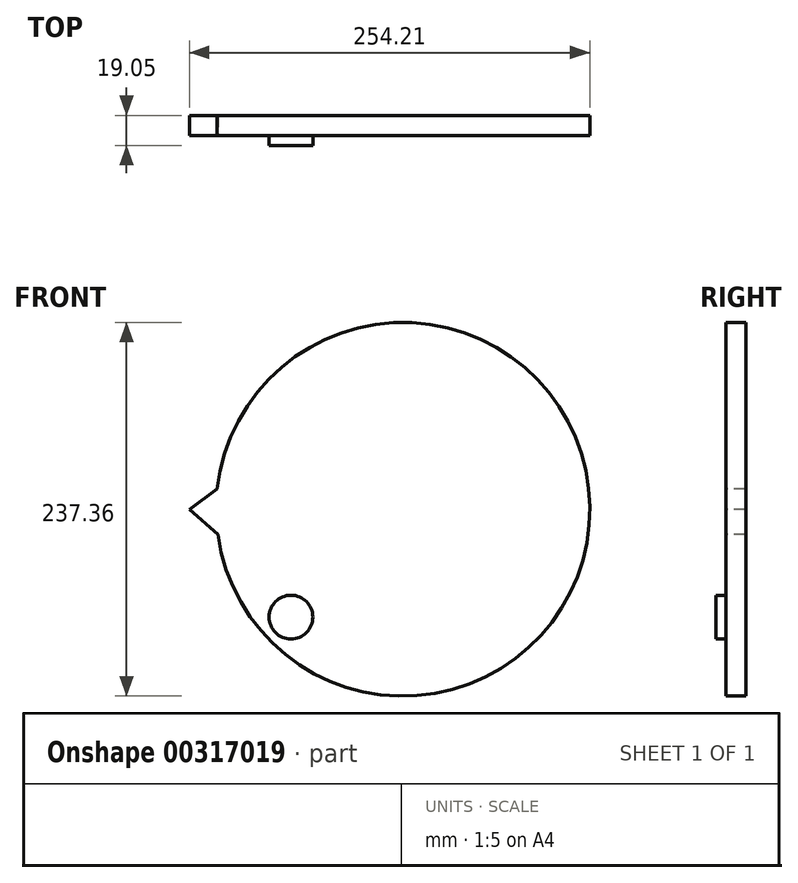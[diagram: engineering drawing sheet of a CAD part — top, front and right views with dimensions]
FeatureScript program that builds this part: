
annotation { "Feature Type Name" : "Feature", "Feature Type Description" : "" }
export const myFeature = defineFeature(function(context is Context, id is Id, definition is map)
    precondition{}
    {
        {
            var Q0;
            Q0=qCreatedBy(makeId("Front.planeOp"),FACE);
            var sketch = newSketch(context, id + "F0", { "sketchPlane" : qUnion([Q0])});
            skCircle(sketch, "E0", {"center": v(0, 0) * mm, "radius": 118.68 * mm});
            skSolve(sketch);
        }
        {
            var Q0;
            Q0 = qSketchRegion(id + "F0", true);
            extrude(context, id + "F1", {"entities" : qUnion([Q0]), "depth" : 12.7 * mm, "symmetric" : true});
        }
        {
            var Q0;
            Q0=makeQuery(id+"F1.opExtrude","CAP_FACE",FACE,{"disambiguationData":[OSD([sQuery(id+"F0.wireOp",EDGE,"E0")])],"isStart":false});
            var sketch = newSketch(context, id + "F2", { "sketchPlane" : qUnion([Q0])});
            skCircle(sketch, "E1", {"center": v(-71.15, -68.46) * mm, "radius": 13.87 * mm});
            skSolve(sketch);
        }
        {
            var Q0;
            Q0 = qSketchRegion(id + "F2", true);
            extrude(context, id + "F3", {"entities" : qUnion([Q0]), "operationType" : NewBodyOperationType.ADD, "depth" : 6.35 * mm});
        }
        {
            var Q0;
            Q0=makeQuery(id+"F1.opExtrude","CAP_FACE",FACE,{"disambiguationData":[OSD([sQuery(id+"F0.wireOp",EDGE,"E0")])],"isStart":false});
            var sketch = newSketch(context, id + "F4", { "sketchPlane" : qUnion([Q0])});
            skLineSegment(sketch, "E2", {"start": v(-117.58, -16.11) * mm, "end": v(-135.53, 0) * mm});
            skLineSegment(sketch, "E3", {"start": v(-135.53, 0) * mm, "end": v(-117.97, 12.9) * mm});
            skArc(sketch, "E4.0", {"start": v(-117.97, 12.9) * mm, "mid": v(-118.67, -1.61) * mm, "end": v(-117.58, -16.11) * mm});
            skSolve(sketch);
        }
        {
            var Q0;
            Q0 = qSketchRegion(id + "F4", true);
            var Q1;
            Q1=makeQuery(id+"F1.opExtrude","CAP_FACE",FACE,{"disambiguationData":[OSD([sQuery(id+"F0.wireOp",EDGE,"E0")])],"isStart":true});
            extrude(context, id + "F5", {"entities" : qUnion([Q0]), "operationType" : NewBodyOperationType.ADD, "endBound" : BoundingType.UP_TO_SURFACE, "oppositeDirection" : true, "endBoundEntityFace" : qUnion([Q1]), "depth" : 25.4 * mm});
        }
    });
